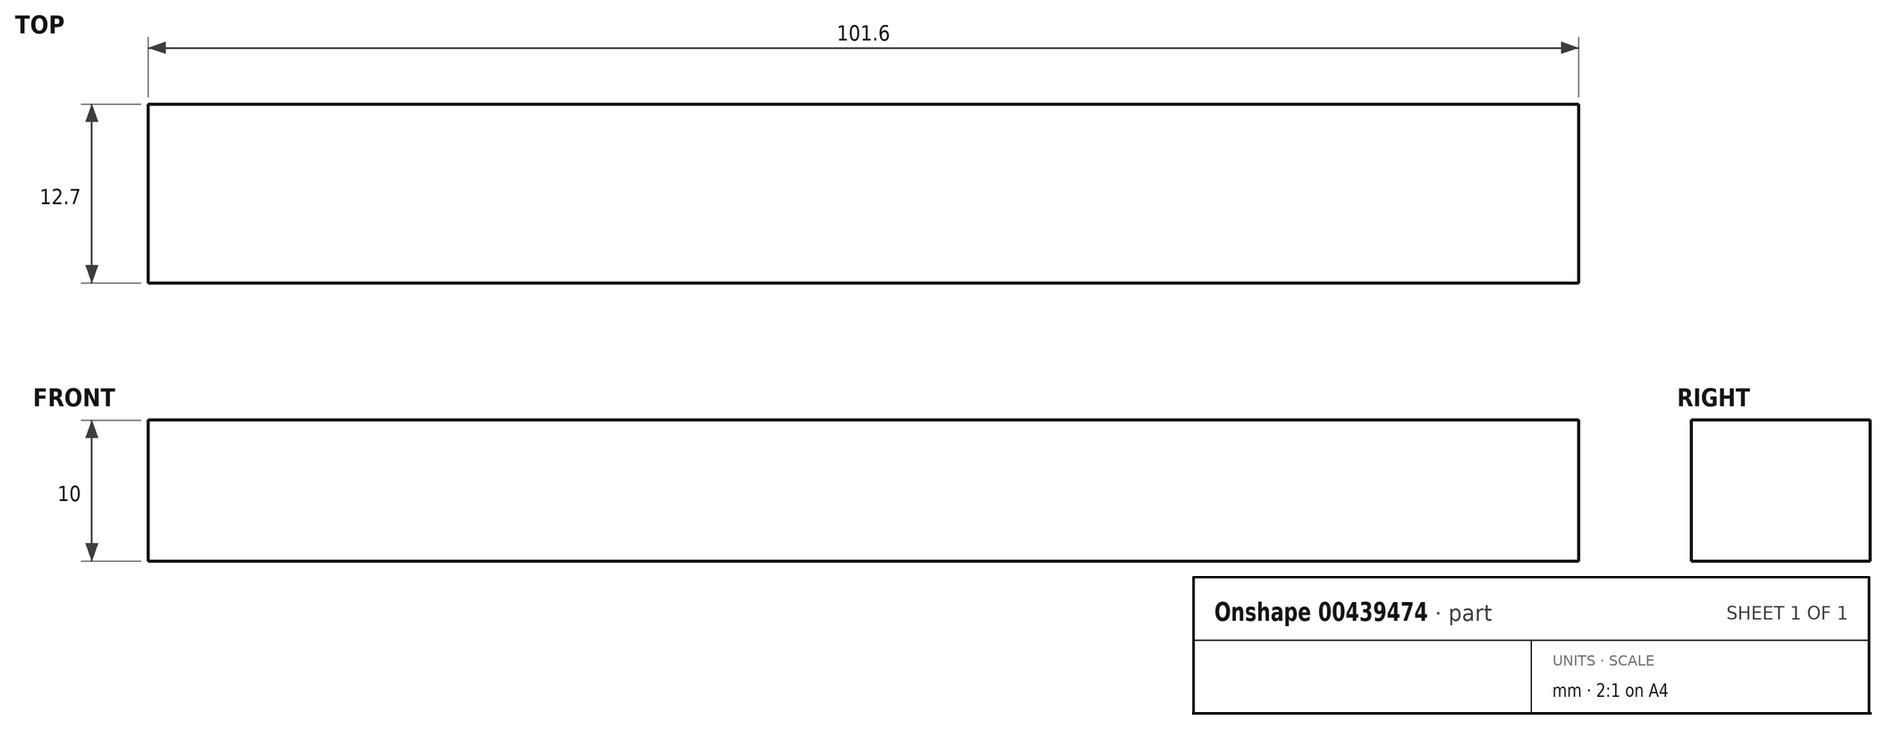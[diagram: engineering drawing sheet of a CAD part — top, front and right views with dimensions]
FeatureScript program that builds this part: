
annotation { "Feature Type Name" : "Feature", "Feature Type Description" : "" }
export const myFeature = defineFeature(function(context is Context, id is Id, definition is map)
    precondition{}
    {
        {
            var Q0;
            Q0=qCreatedBy(makeId("Front.planeOp"),FACE);
            var sketch = newSketch(context, id + "F0", { "sketchPlane" : qUnion([Q0])});
            skLineSegment(sketch, "E0.bottom", {"start": v(-50.8, 5) * mm, "end": v(50.8, 5) * mm});
            skLineSegment(sketch, "E0.top", {"start": v(-50.8, -5) * mm, "end": v(50.8, -5) * mm});
            skLineSegment(sketch, "E0.left", {"start": v(-50.8, 5) * mm, "end": v(-50.8, -5) * mm});
            skLineSegment(sketch, "E0.right", {"start": v(50.8, 5) * mm, "end": v(50.8, -5) * mm});
            skPoint(sketch, "E0.middle", {"position": v(0, 0) * mm});
            skSolve(sketch);
        }
        {
            var Q0;
            Q0 = qSketchRegion(id + "F0", true);
            extrude(context, id + "F1", {"entities" : qUnion([Q0]), "depth" : 12.7 * mm});
        }
    });
